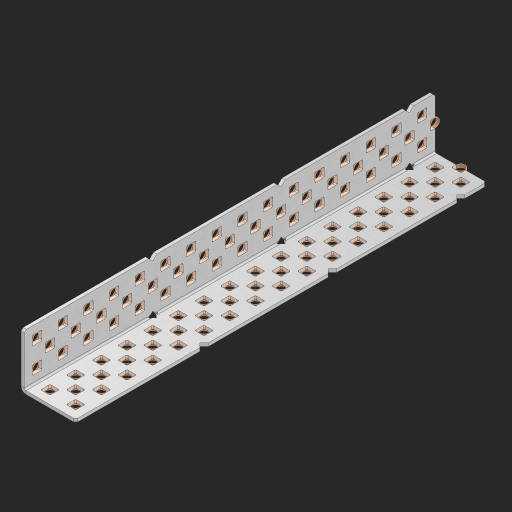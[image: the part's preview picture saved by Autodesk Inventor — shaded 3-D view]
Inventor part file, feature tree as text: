
AUTODESK INVENTOR PART (.ipt)
format: ipt  version: 2023 (Build 270158000, 158)  size: 1,334,784 bytes
history: native  units: in
note: dims shown in document units (in); Inventor stores cm internally (conversion verified against a paired STEP export)
features: other x102, extrude x94, sheet_metal_op x8, sketch x7, pattern_linear x2, mirror x1, chamfer x1
ambient origin geometry x8: Origin, YZ Plane, XZ Plane, XY Plane, X Axis, Y Axis, Z Axis, Center Point
bodies: Solid1 (feature_tree), Body (feature_tree)
feature tree (215):
  sheet_metal_op  "Flanges"
  sheet_metal_op  "Body Pattern"
  pattern_linear  "Center Pattern"  Spacing1=1.0in  [1 undecoded]
  other  "Arc Length"
  pattern_linear  "Notch Pattern"  Spacing1=0.25in  [1 undecoded]
  other  "Diagonal Plane"
  mirror  "Everything Mirrored"
  chamfer  "End Chamfer"
  sketch  "Sketch1"  dims[d0=1.0in]
  other  "Plate1"
  sketch  "Sketch2"  dims[d1=8.0in]
  other  "Plate2"
  sheet_metal_op  "Bend1"
  sheet_metal_op  "Corner1"
  sketch  "Sketch8"  dims[d2=0.0625in]
  sketch  "Sketch9"  dims[d3=0.0625in]
  other  "Srf91"
  sheet_metal_op  "Body Pattern Sketch"
  other  "Srf92"
  sketch  "Sketch13"  dims[d4=0.0312in]
  sketch  "Sketch15"  dims[d5=0.125in]
  sketch  "Sketch16"  dims[d6=0.0625in d7=1.0in d8=90.0deg d9=0.0312in d10=0.25in d11=0.0625in d12=0.0625in d49=0.182in d50=0.02in d52=0.25in d53=0.0625in d54=0.0in d55=0.172in d56=1.0in d57=0.0in d60=6.2992in d62=0.5in d63=0.7874in d65=0.5in d85=0.1473in d86=0.1782in d89=0.0625in d90=0.0in d91=0.04in d92=0.0491in d95=2.5in d96=0.04in d97=0.25in d98=45.0deg d99=0.25in d106=0.182in d107=0.02in d108=0.5in d110=0.0625in d111=0.0in d112=0.172in d113=0.5in d114=0.0in d117=0.5in d123=0.25in d125=0.25in d126=0.0491in d127=0.1473in d128=0.08in d129=0.04in d130=2.5in]
  other  "Srf786"
  other  "Srf856"
  other  "Srf857"
  other  "Srf858"
  other  "Srf859"
  other  "Srf860"
  other  "Srf861"
  other  "Srf889"
  other  "Srf890"
  other  "Srf891"
  other  "Srf1275"
  other  "Srf1276"
  other  "Srf1278"
  other  "Srf1279"
  other  "Srf1280"
  other  "Srf1281"
  other  "Srf1282"
  other  "Srf1283"
  other  "Srf1277"
  other  "Srf1285"
  other  "Srf1286"
  other  "Srf1287"
  other  "Srf1383"
  other  "Srf1384"
  other  "Srf1385"
  other  "Srf1386"
  other  "Srf1387"
  other  "Srf1388"
  other  "Srf1389"
  other  "Srf1390"
  other  "Srf1391"
  other  "Srf1392"
  other  "Srf1393"
  other  "Srf1394"
  other  "Srf1395"
  other  "Srf1396"
  other  "Srf1397"
  other  "Srf1398"
  other  "Srf1399"
  other  "Srf1400"
  other  "Srf1401"
  other  "Srf1402"
  other  "Srf1403"
  other  "Srf1404"
  other  "Srf1405"
  other  "Srf1406"
  other  "Srf1445"
  other  "Srf1446"
  other  "Srf1447"
  other  "Srf1448"
  other  "Srf1449"
  other  "Srf1450"
  other  "Srf1451"
  other  "Srf1452"
  other  "Srf1453"
  other  "Srf1454"
  other  "Srf1455"
  other  "Srf1456"
  other  "Srf1475"
  other  "Srf1476"
  other  "Srf1477"
  other  "Srf1478"
  other  "Srf1479"
  other  "Srf1480"
  other  "Srf1481"
  other  "Srf1482"
  other  "Srf1483"
  other  "Srf1484"
  other  "Srf1485"
  other  "Srf1486"
  other  "Srf1487"
  other  "Srf1488"
  other  "Srf1489"
  other  "Srf1490"
  other  "Srf1491"
  other  "Srf1492"
  other  "Srf1493"
  other  "Srf1494"
  other  "Srf1495"
  other  "Srf1496"
  other  "Srf1497"
  other  "Srf1498"
  other  "Srf1537"
  other  "Srf1538"
  other  "Srf1539"
  other  "Srf1540"
  other  "Srf1541"
  other  "Srf1542"
  other  "Srf1543"
  other  "Srf1544"
  other  "Srf1545"
  other  "Srf1546"
  other  "Srf1547"
  other  "Srf1548"
  sheet_metal_op  "Body Stamp"
  sheet_metal_op  "Body Circle"
  other  "Center Stamp"
  other  "Center Circle"
  sheet_metal_op  "Notch"
  extrude  "ExtrusionSrf92"  Depth=0.0625in
  extrude  "ExtrusionSrf856"  Depth=0.0625in
  extrude  "ExtrusionSrf857"  Depth=0.182in
  extrude  "ExtrusionSrf858"  Depth=0.02in
  extrude  "ExtrusionSrf859"  Depth=0.25in
  extrude  "ExtrusionSrf860"  Depth=0.0625in
  extrude  "ExtrusionSrf861"  TaperAngle=0.0deg  [1 undecoded]
  extrude  "ExtrusionSrf889"  Depth=2.5in
  extrude  "ExtrusionSrf890"  Depth=1.0in TaperAngle=0.0deg
  extrude  "ExtrusionSrf891"  Depth=2.5in
  extrude  "ExtrusionSrf1275"  Depth=0.5in
  extrude  "ExtrusionSrf1276"  Depth=2.5in
  extrude  "ExtrusionSrf1277"  Depth=2.5in
  extrude  "ExtrusionSrf1278"  Depth=0.0625in
  extrude  "ExtrusionSrf1279"  Depth=2.5in TaperAngle=0.0deg
  extrude  "ExtrusionSrf1280"  Depth=2.5in
  extrude  "ExtrusionSrf1281"  Depth=0.25in TaperAngle=45.0deg
  extrude  "ExtrusionSrf1282"  Depth=0.25in
  extrude  "ExtrusionSrf1345"  Depth=0.182in
  extrude  "ExtrusionSrf1346"  Depth=0.02in
  extrude  "ExtrusionSrf1347"  Depth=0.5in
  extrude  "ExtrusionSrf1348"  Depth=0.0625in
  extrude  "ExtrusionSrf1383"  TaperAngle=0.0deg  [1 undecoded]
  extrude  "ExtrusionSrf1384"  Depth=2.5in
  extrude  "ExtrusionSrf1385"  Depth=0.5in TaperAngle=0.0deg
  extrude  "ExtrusionSrf1386"  Depth=0.5in
  extrude  "ExtrusionSrf1387"  Depth=0.25in
  extrude  "ExtrusionSrf1388"  Depth=0.25in
  extrude  "ExtrusionSrf1389"  Depth=2.5in
  extrude  "ExtrusionSrf1390"  Depth=2.5in
  extrude  "ExtrusionSrf1391"  Depth=2.5in
  extrude  "ExtrusionSrf1392"  Depth=2.5in
  extrude  "ExtrusionSrf1393"  Depth=2.5in
  extrude  "ExtrusionSrf1394"  [1 undecoded]
  extrude  "ExtrusionSrf1395"  [1 undecoded]
  extrude  "ExtrusionSrf1396"  [1 undecoded]
  extrude  "ExtrusionSrf1397"  [1 undecoded]
  extrude  "ExtrusionSrf1398"  [1 undecoded]
  extrude  "ExtrusionSrf1399"  [1 undecoded]
  extrude  "ExtrusionSrf1400"  [1 undecoded]
  extrude  "ExtrusionSrf1401"  [1 undecoded]
  extrude  "ExtrusionSrf1402"  [1 undecoded]
  extrude  "ExtrusionSrf1403"  [1 undecoded]
  extrude  "ExtrusionSrf1404"  [1 undecoded]
  extrude  "ExtrusionSrf1405"  [1 undecoded]
  extrude  "ExtrusionSrf1406"  [1 undecoded]
  extrude  "ExtrusionSrf1445"  [1 undecoded]
  extrude  "ExtrusionSrf1446"  [1 undecoded]
  extrude  "ExtrusionSrf1447"  [1 undecoded]
  extrude  "ExtrusionSrf1448"  [1 undecoded]
  extrude  "ExtrusionSrf1449"  [1 undecoded]
  extrude  "ExtrusionSrf1450"  [1 undecoded]
  extrude  "ExtrusionSrf1451"  [1 undecoded]
  extrude  "ExtrusionSrf1452"  [1 undecoded]
  extrude  "ExtrusionSrf1453"  [1 undecoded]
  extrude  "ExtrusionSrf1454"  [1 undecoded]
  extrude  "ExtrusionSrf1455"  [1 undecoded]
  extrude  "ExtrusionSrf1456"  [1 undecoded]
  extrude  "ExtrusionSrf1475"  [1 undecoded]
  extrude  "ExtrusionSrf1476"  [1 undecoded]
  extrude  "ExtrusionSrf1477"  [1 undecoded]
  extrude  "ExtrusionSrf1478"  [1 undecoded]
  extrude  "ExtrusionSrf1479"  [1 undecoded]
  extrude  "ExtrusionSrf1480"  [1 undecoded]
  extrude  "ExtrusionSrf1481"  [1 undecoded]
  extrude  "ExtrusionSrf1482"  [1 undecoded]
  extrude  "ExtrusionSrf1483"  [1 undecoded]
  extrude  "ExtrusionSrf1484"  [1 undecoded]
  extrude  "ExtrusionSrf1485"  [1 undecoded]
  extrude  "ExtrusionSrf1486"  [1 undecoded]
  extrude  "ExtrusionSrf1487"  [1 undecoded]
  extrude  "ExtrusionSrf1488"  [1 undecoded]
  extrude  "ExtrusionSrf1489"  [1 undecoded]
  extrude  "ExtrusionSrf1490"  [1 undecoded]
  extrude  "ExtrusionSrf1491"  [1 undecoded]
  extrude  "ExtrusionSrf1492"  [1 undecoded]
  extrude  "ExtrusionSrf1493"  [1 undecoded]
  extrude  "ExtrusionSrf1494"  [1 undecoded]
  extrude  "ExtrusionSrf1495"  [1 undecoded]
  extrude  "ExtrusionSrf1496"  [1 undecoded]
  extrude  "ExtrusionSrf1497"  [1 undecoded]
  extrude  "ExtrusionSrf1498"  [1 undecoded]
  extrude  "ExtrusionSrf1537"  [1 undecoded]
  extrude  "ExtrusionSrf1538"  [1 undecoded]
  extrude  "ExtrusionSrf1539"  [1 undecoded]
  extrude  "ExtrusionSrf1540"  [1 undecoded]
  extrude  "ExtrusionSrf1541"  [1 undecoded]
  extrude  "ExtrusionSrf1542"  [1 undecoded]
  extrude  "ExtrusionSrf1543"  [1 undecoded]
  extrude  "ExtrusionSrf1544"  [1 undecoded]
  extrude  "ExtrusionSrf1545"  [1 undecoded]
  extrude  "ExtrusionSrf1546"  [1 undecoded]
  extrude  "ExtrusionSrf1547"  [1 undecoded]
  extrude  "ExtrusionSrf1548"  [1 undecoded]
note: 65 required parameter values undecoded (feature->parameter linkage not recoverable at this tier; creation-order binding heuristic only, values carry confidence <= 0.55)
